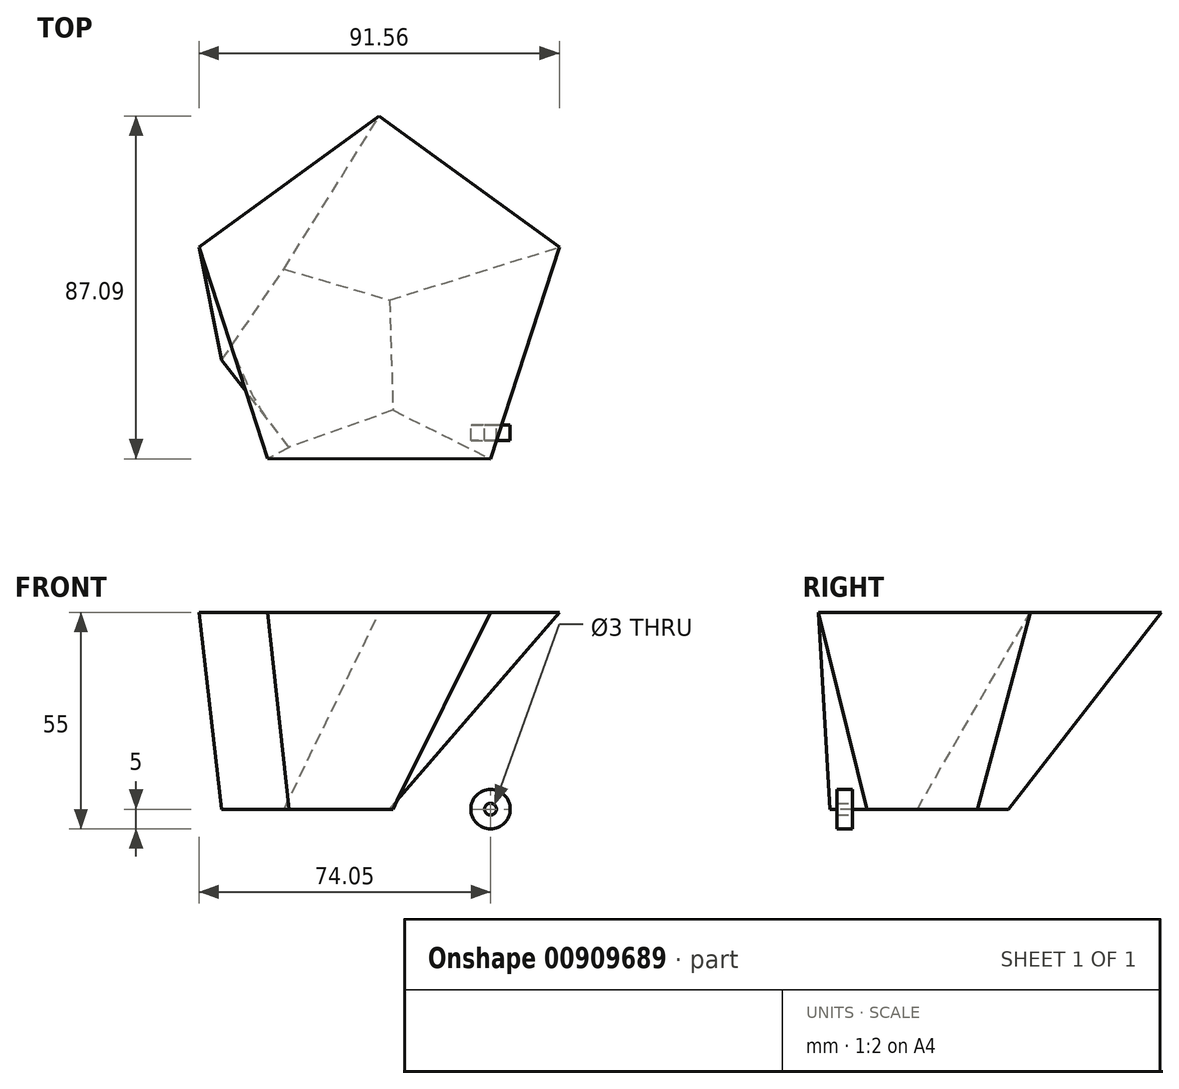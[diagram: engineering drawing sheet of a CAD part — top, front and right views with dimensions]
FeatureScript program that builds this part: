
annotation { "Feature Type Name" : "Feature", "Feature Type Description" : "" }
export const myFeature = defineFeature(function(context is Context, id is Id, definition is map)
    precondition{}
    {
        {
            var Q0;
            Q0=qCreatedBy(makeId("Front.planeOp"),FACE);
            var sketch = newSketch(context, id + "F0", { "sketchPlane" : qUnion([Q0])});
            skCircle(sketch, "E0", {"center": v(0, 0) * mm, "radius": 5 * mm});
            skCircle(sketch, "E1", {"center": v(0, 0) * mm, "radius": 1.5 * mm});
            skLineSegment(sketch, "E2.bottom", {"start": v(-9.2, -8.74) * mm, "end": v(0.8, -8.74) * mm});
            skLineSegment(sketch, "E2.top", {"start": v(-9.2, -15.05) * mm, "end": v(0.8, -15.05) * mm});
            skLineSegment(sketch, "E2.left", {"start": v(-9.2, -8.74) * mm, "end": v(-9.2, -15.05) * mm});
            skLineSegment(sketch, "E2.right", {"start": v(0.8, -8.74) * mm, "end": v(0.8, -15.05) * mm});
            skSolve(sketch);
        }
        {
            var Q0;
            Q0=makeQuery(id+"F0.imprint","IMPRINT",FACE,{"disambiguationData":[TD([[makeQuery(id+"F0.imprint","IMPRINT",EDGE,{"derivedFrom":sQuery(id+"F0.wireOp",EDGE,"E0")}),1.0]])]});
            extrude(context, id + "F1", {"entities" : qUnion([Q0]), "depth" : 4 * mm, "offsetDistance" : 25 * mm});
        }
        {
            var Q0;
            Q0=qCreatedBy(makeId("Top.planeOp"),FACE);
            var sketch = newSketch(context, id + "F2", { "sketchPlane" : qUnion([Q0])});
            skCircle(sketch, "E3.cCircle", {"center": v(-44.46, 17.14) * mm, "radius": 23.82 * mm, "construction": true});
            skLineSegment(sketch, "E3.0", {"start": v(-24.8, 3.7) * mm, "end": v(-51.16, -5.72) * mm});
            skLineSegment(sketch, "E3.1", {"start": v(-51.16, -5.72) * mm, "end": v(-68.27, 16.45) * mm});
            skLineSegment(sketch, "E3.2", {"start": v(-68.27, 16.45) * mm, "end": v(-52.47, 39.57) * mm});
            skLineSegment(sketch, "E3.3", {"start": v(-52.47, 39.57) * mm, "end": v(-25.6, 31.69) * mm});
            skLineSegment(sketch, "E3.4", {"start": v(-25.6, 31.69) * mm, "end": v(-24.8, 3.7) * mm});
            skSolve(sketch);
        }
        {
            var Q0;
            Q0=qCreatedBy(makeId("Top.planeOp"),FACE);
            cPlane(context, id + "F3", {"entities" : qUnion([Q0]), "cplaneType" : CPlaneType.OFFSET, "offset" : 50 * mm, "width" : 150 * mm, "height" : 150 * mm});
        }
        {
            var Q0;
            Q0=qCreatedBy(id+"F3.planeOp",FACE);
            var sketch = newSketch(context, id + "F4", { "sketchPlane" : qUnion([Q0])});
            skCircle(sketch, "E4.cCircle", {"center": v(-28.27, 30.3) * mm, "radius": 38.94 * mm, "construction": true});
            skLineSegment(sketch, "E4.0", {"start": v(0, -8.66) * mm, "end": v(-56.59, -8.63) * mm});
            skLineSegment(sketch, "E4.1", {"start": v(-56.59, -8.63) * mm, "end": v(-74.05, 45.2) * mm});
            skLineSegment(sketch, "E4.2", {"start": v(-74.05, 45.2) * mm, "end": v(-28.25, 78.43) * mm});
            skLineSegment(sketch, "E4.3", {"start": v(-28.25, 78.43) * mm, "end": v(17.5, 45.15) * mm});
            skLineSegment(sketch, "E4.4", {"start": v(17.5, 45.15) * mm, "end": v(0, -8.66) * mm});
            skPoint(sketch, "E4.0.midPoint", {"position": v(-28.3, -8.64) * mm});
            skSolve(sketch);
        }
        {
            var Q0;
            Q0=makeQuery(id+"F2.imprint","IMPRINT",FACE,{"disambiguationData":[TD([[makeQuery(id+"F2.imprint","IMPRINT",EDGE,{"derivedFrom":sQuery(id+"F2.wireOp",EDGE,"E3.0")}),-1.0]])]});
            var Q1;
            Q1=makeQuery(id+"F4.imprint","IMPRINT",FACE,{"disambiguationData":[TD([[makeQuery(id+"F4.imprint","IMPRINT",EDGE,{"derivedFrom":sQuery(id+"F4.wireOp",EDGE,"E4.0")}),-1.0]])]});
            loft(context, id + "F5", {"sheetProfilesArray" : [{ "sheetProfileEntities" : qUnion([Q0]) }, { "sheetProfileEntities" : qUnion([Q1]) }]});
        }
    });
